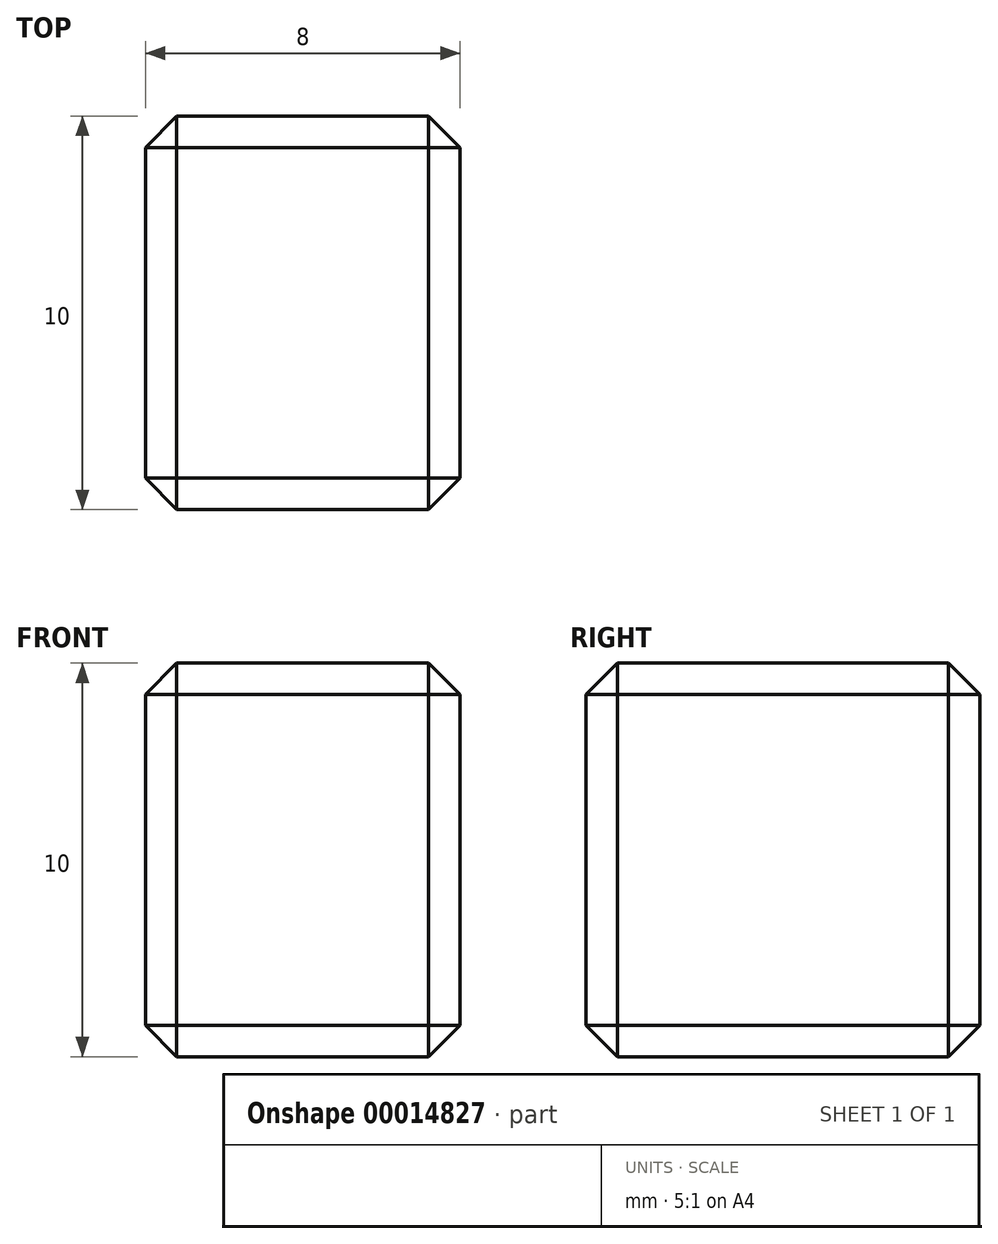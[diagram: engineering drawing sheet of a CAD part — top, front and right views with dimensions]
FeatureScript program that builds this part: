
annotation { "Feature Type Name" : "Feature", "Feature Type Description" : "" }
export const myFeature = defineFeature(function(context is Context, id is Id, definition is map)
    precondition{}
    {
        {
            var Q0;
            Q0=qCreatedBy(makeId("Top.planeOp"),FACE);
            var sketch = newSketch(context, id + "F0", { "sketchPlane" : qUnion([Q0])});
            skLineSegment(sketch, "E0.bottom", {"start": v(0, 0) * mm, "end": v(8, 0) * mm});
            skLineSegment(sketch, "E0.top", {"start": v(0, 10) * mm, "end": v(8, 10) * mm});
            skLineSegment(sketch, "E0.left", {"start": v(0, 0) * mm, "end": v(0, 10) * mm});
            skLineSegment(sketch, "E0.right", {"start": v(8, 0) * mm, "end": v(8, 10) * mm});
            skSolve(sketch);
        }
        {
            var Q0;
            Q0 = qSketchRegion(id + "F0", true);
            extrude(context, id + "F1", {"entities" : qUnion([Q0]), "depth" : 10 * mm});
        }
        {
            var Q0;
            Q0=makeQuery(id+"F1.opExtrude","SWEPT_FACE",FACE,{"disambiguationData":[OSD([sQuery(id+"F0.wireOp",EDGE,"E0.bottom")])]});
            var Q1;
            Q1=makeQuery(id+"F1.opExtrude","SWEPT_FACE",FACE,{"disambiguationData":[OSD([sQuery(id+"F0.wireOp",EDGE,"E0.top")])]});
            var Q2;
            Q2=makeQuery(id+"F1.opExtrude","CAP_EDGE",EDGE,{"disambiguationData":[OSD([sQuery(id+"F0.wireOp",EDGE,"E0.right")])],"isStart":false});
            var Q3;
            Q3=makeQuery(id+"F1.opExtrude","CAP_EDGE",EDGE,{"disambiguationData":[OSD([sQuery(id+"F0.wireOp",EDGE,"E0.left")])],"isStart":false});
            var Q4;
            Q4=makeQuery(id+"F1.opExtrude","CAP_EDGE",EDGE,{"disambiguationData":[OSD([sQuery(id+"F0.wireOp",EDGE,"E0.right")])],"isStart":true});
            var Q5;
            Q5=makeQuery(id+"F1.opExtrude","CAP_EDGE",EDGE,{"disambiguationData":[OSD([sQuery(id+"F0.wireOp",EDGE,"E0.left")])],"isStart":true});
            chamfer(context, id + "F2", {"entities" : qUnion([Q0, Q1, Q2, Q3, Q4, Q5]), "width" : .8 * mm, "tangentPropagation" : true});
        }
    });
